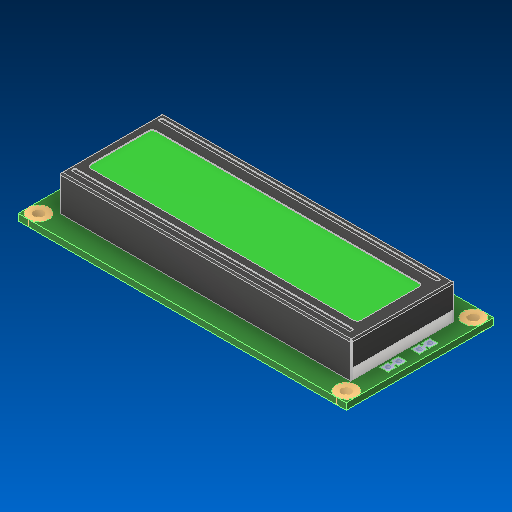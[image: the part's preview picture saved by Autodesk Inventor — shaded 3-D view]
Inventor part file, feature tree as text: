
AUTODESK INVENTOR PART (.ipt)
format: ipt  version: 2019 (Build 230136000, 136)  size: 564,224 bytes
history: native  units: mm
features: other x31, fillet x3
ambient origin geometry x8: Origin, YZ Plane, XZ Plane, XY Plane, X Axis, Y Axis, Z Axis, Center Point
bodies: Solid1 (feature_tree), Solid2 (feature_tree), Solid3 (feature_tree), Solid4 (feature_tree), Solid5 (feature_tree), Solid6 (feature_tree), Solid7 (feature_tree), Solid8 (feature_tree), Solid9 (feature_tree), Solid10 (feature_tree), Solid11 (feature_tree), Solid12 (feature_tree), Solid13 (feature_tree), Solid14 (feature_tree), Solid15 (feature_tree), Solid16 (feature_tree), Solid17 (feature_tree), Solid18 (feature_tree), Solid19 (feature_tree), Solid20 (feature_tree), Solid21 (feature_tree), Solid22 (feature_tree), Solid23 (feature_tree), Solid24 (feature_tree), Solid25 (feature_tree), Solid26 (feature_tree), Solid27 (feature_tree), Solid28 (feature_tree), Solid29 (feature_tree), Solid30 (feature_tree), Solid31 (feature_tree), Solid32 (feature_tree), Solid33 (feature_tree), Solid34 (feature_tree)
feature tree (34):
  other  "Cut-Extrude2"
  other  "Boss-Extrude3"
  other  "Boss-Extrude7[1]"
  other  "Boss-Extrude7[2]"
  other  "Boss-Extrude7[3]"
  other  "Boss-Extrude7[4]"
  other  "Boss-Extrude7[5]"
  other  "LPattern3[1]"
  other  "LPattern3[2]"
  other  "LPattern3[3]"
  other  "LPattern3[4]"
  other  "LPattern3[5]"
  other  "LPattern3[6]"
  other  "LPattern3[7]"
  other  "LPattern3[8]"
  other  "LPattern3[9]"
  other  "LPattern3[10]"
  other  "LPattern3[11]"
  other  "LPattern3[12]"
  other  "LPattern3[13]"
  other  "LPattern3[14]"
  other  "LPattern3[15]"
  fillet  "Fillet5"  [1 undecoded]
  fillet  "Fillet7"  [1 undecoded]
  fillet  "Fillet9"  [1 undecoded]
  other  "Boss-Extrude9[1]"
  other  "Boss-Extrude9[2]"
  other  "Boss-Extrude9[3]"
  other  "Boss-Extrude9[4]"
  other  "Boss-Extrude9[5]"
  other  "Boss-Extrude9[6]"
  other  "Cut-Extrude6"
  other  "Boss-Extrude12[1]"
  other  "Boss-Extrude12[2]"
note: 3 required parameter values undecoded (feature->parameter linkage not recoverable at this tier; creation-order binding heuristic only, values carry confidence <= 0.55)
